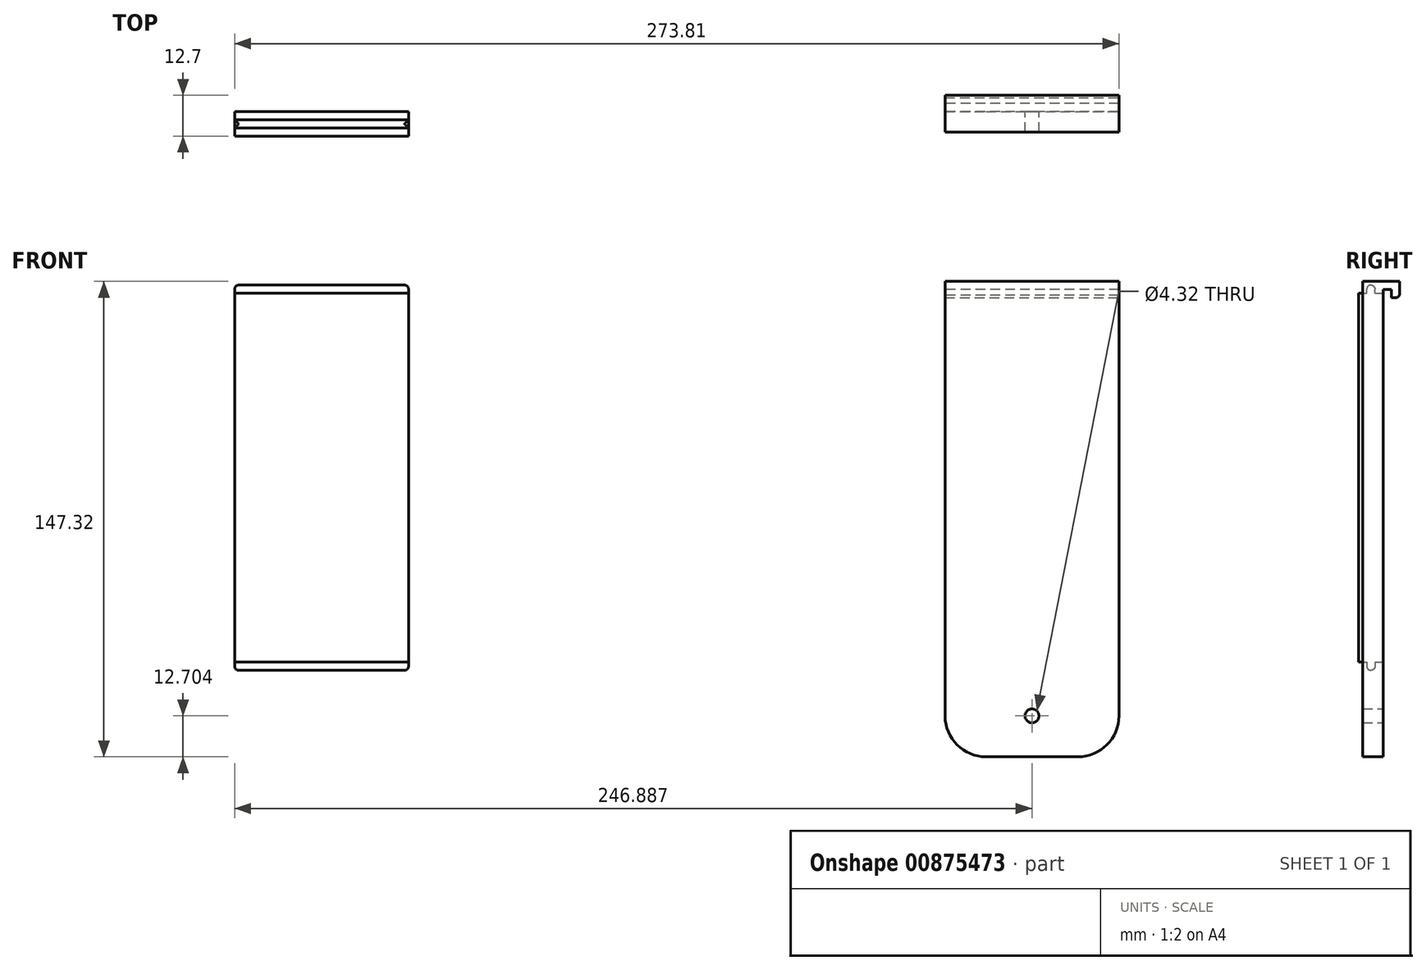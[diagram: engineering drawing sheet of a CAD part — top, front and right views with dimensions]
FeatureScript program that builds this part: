
annotation { "Feature Type Name" : "Feature", "Feature Type Description" : "" }
export const myFeature = defineFeature(function(context is Context, id is Id, definition is map)
    precondition{}
    {
        {
            var Q0;
            Q0=qCreatedBy(makeId("Front.planeOp"),FACE);
            var sketch = newSketch(context, id + "F0", { "sketchPlane" : qUnion([Q0])});
            skLineSegment(sketch, "E0.bottom", {"start": v(-137.16, 59.7) * mm, "end": v(-83.32, 59.7) * mm});
            skLineSegment(sketch, "E0.top", {"start": v(-137.16, -54.6) * mm, "end": v(-83.32, -54.6) * mm});
            skLineSegment(sketch, "E0.left", {"start": v(-137.16, 59.7) * mm, "end": v(-137.16, -54.6) * mm});
            skLineSegment(sketch, "E0.right", {"start": v(-83.32, 59.7) * mm, "end": v(-83.32, -54.6) * mm});
            skSolve(sketch);
        }
        {
            var Q0;
            Q0=makeQuery(id+"F0.imprint","IMPRINT",FACE,{"disambiguationData":[TD([[makeQuery(id+"F0.imprint","IMPRINT",EDGE,{"derivedFrom":sQuery(id+"F0.wireOp",EDGE,"E0.bottom")}),-1.0]])]});
            extrude(context, id + "F1", {"entities" : qUnion([Q0]), "depth" : 7.62 * mm, "offsetDistance" : 25.4 * mm});
        }
        {
            var Q0;
            Q0=makeQuery(id+"F1.opExtrude","SWEPT_FACE",FACE,{"disambiguationData":[OSD([sQuery(id+"F0.wireOp",EDGE,"E0.left")])]});
            var sketch = newSketch(context, id + "F2", { "sketchPlane" : qUnion([Q0])});
            skLineSegment(sketch, "E1.bottom", {"start": v(2.54, -54.6) * mm, "end": v(5.08, -54.6) * mm});
            skLineSegment(sketch, "E1.top", {"start": v(2.54, -57.13) * mm, "end": v(5.08, -57.13) * mm});
            skLineSegment(sketch, "E1.left", {"start": v(2.54, -54.6) * mm, "end": v(2.54, -57.13) * mm});
            skLineSegment(sketch, "E1.right", {"start": v(5.08, -54.6) * mm, "end": v(5.08, -57.13) * mm});
            skLineSegment(sketch, "E2.bottom", {"start": v(2.54, 59.7) * mm, "end": v(5.08, 59.7) * mm});
            skLineSegment(sketch, "E2.top", {"start": v(2.54, 62.25) * mm, "end": v(5.08, 62.25) * mm});
            skLineSegment(sketch, "E2.left", {"start": v(2.54, 59.7) * mm, "end": v(2.54, 62.25) * mm});
            skLineSegment(sketch, "E2.right", {"start": v(5.08, 59.7) * mm, "end": v(5.08, 62.25) * mm});
            skSolve(sketch);
        }
        {
            var Q0;
            Q0=makeQuery(id+"F2.imprint","IMPRINT",FACE,{"disambiguationData":[TD([[makeQuery(id+"F2.imprint","IMPRINT",EDGE,{"derivedFrom":sQuery(id+"F2.wireOp",EDGE,"E1.bottom")}),1.0]])]});
            var Q1;
            Q1=makeQuery(id+"F2.imprint","IMPRINT",FACE,{"disambiguationData":[TD([[makeQuery(id+"F2.imprint","IMPRINT",EDGE,{"derivedFrom":sQuery(id+"F2.wireOp",EDGE,"E2.bottom")}),-1.0]])]});
            extrude(context, id + "F3", {"entities" : qUnion([Q0, Q1]), "operationType" : NewBodyOperationType.ADD, "oppositeDirection" : true, "depth" : 53.85 * mm, "offsetDistance" : 25.4 * mm});
        }
        {
            var Q0;
            Q0=makeQuery(id+"F3.opExtrude","SWEPT_EDGE",EDGE,{"disambiguationData":[OSD([sQuery(id+"F2.wireOp",EDGE,"E2.top"),sQuery(id+"F2.wireOp",EDGE,"E2.left")])]});
            var Q1;
            Q1=makeQuery(id+"F3.opExtrude","SWEPT_EDGE",EDGE,{"disambiguationData":[OSD([sQuery(id+"F2.wireOp",EDGE,"E2.top"),sQuery(id+"F2.wireOp",EDGE,"E2.right")])]});
            var Q2;
            Q2=makeQuery(id+"F3.opExtrude","CAP_EDGE",EDGE,{"disambiguationData":[OSD([sQuery(id+"F2.wireOp",EDGE,"E2.top")])],"isStart":true});
            var Q3;
            Q3=makeQuery(id+"F3.opExtrude","CAP_EDGE",EDGE,{"disambiguationData":[OSD([sQuery(id+"F2.wireOp",EDGE,"E2.top")])],"isStart":false});
            fillet(context, id + "F4", {"entities" : qUnion([Q0, Q1, Q2, Q3]), "radius" : 1.27 * mm, "tangentPropagation" : true, "allowEdgeOverflow" : false});
        }
        {
            var Q0;
            Q0=makeQuery(id+"F3.opExtrude","SWEPT_EDGE",EDGE,{"disambiguationData":[OSD([sQuery(id+"F2.wireOp",EDGE,"E1.top"),sQuery(id+"F2.wireOp",EDGE,"E1.right")])]});
            var Q1;
            Q1=makeQuery(id+"F3.opExtrude","SWEPT_EDGE",EDGE,{"disambiguationData":[OSD([sQuery(id+"F2.wireOp",EDGE,"E1.top"),sQuery(id+"F2.wireOp",EDGE,"E1.left")])]});
            var Q2;
            Q2=makeQuery(id+"F3.opExtrude","CAP_EDGE",EDGE,{"disambiguationData":[OSD([sQuery(id+"F2.wireOp",EDGE,"E1.top")])],"isStart":false});
            var Q3;
            Q3=makeQuery(id+"F3.opExtrude","CAP_EDGE",EDGE,{"disambiguationData":[OSD([sQuery(id+"F2.wireOp",EDGE,"E1.top")])],"isStart":true});
            fillet(context, id + "F5", {"entities" : qUnion([Q0, Q1, Q2, Q3]), "radius" : 1.27 * mm, "tangentPropagation" : true, "allowEdgeOverflow" : false});
        }
        {
            var Q0;
            Q0=qCreatedBy(makeId("Front.planeOp"),FACE);
            var sketch = newSketch(context, id + "F6", { "sketchPlane" : qUnion([Q0])});
            skLineSegment(sketch, "E3.bottom", {"start": v(82.8, -83.95) * mm, "end": v(136.65, -83.95) * mm});
            skLineSegment(sketch, "E3.top", {"start": v(82.8, 63.37) * mm, "end": v(136.65, 63.37) * mm});
            skLineSegment(sketch, "E3.left", {"start": v(82.8, -83.95) * mm, "end": v(82.8, 63.37) * mm});
            skLineSegment(sketch, "E3.right", {"start": v(136.65, -83.95) * mm, "end": v(136.65, 63.37) * mm});
            skSolve(sketch);
        }
        {
            var Q0;
            Q0=makeQuery(id+"F6.imprint","IMPRINT",FACE,{"disambiguationData":[TD([[makeQuery(id+"F6.imprint","IMPRINT",EDGE,{"derivedFrom":sQuery(id+"F6.wireOp",EDGE,"E3.bottom")}),1.0]])]});
            extrude(context, id + "F7", {"entities" : qUnion([Q0]), "depth" : 6.35 * mm, "offsetDistance" : 25.4 * mm});
        }
        {
            var Q0;
            Q0=makeQuery(id+"F7.opExtrude","SWEPT_EDGE",EDGE,{"disambiguationData":[OSD([sQuery(id+"F6.wireOp",EDGE,"E3.bottom"),sQuery(id+"F6.wireOp",EDGE,"E3.right")])]});
            var Q1;
            Q1=makeQuery(id+"F7.opExtrude","SWEPT_EDGE",EDGE,{"disambiguationData":[OSD([sQuery(id+"F6.wireOp",EDGE,"E3.bottom"),sQuery(id+"F6.wireOp",EDGE,"E3.left")])]});
            fillet(context, id + "F8", {"entities" : qUnion([Q0, Q1]), "radius" : 12.7 * mm, "tangentPropagation" : true, "allowEdgeOverflow" : false});
        }
        {
            var Q0;
            Q0=makeQuery(id+"F7.opExtrude","CAP_FACE",FACE,{"disambiguationData":[OSD([sQuery(id+"F6.wireOp",EDGE,"E3.bottom"),sQuery(id+"F6.wireOp",EDGE,"E3.top"),sQuery(id+"F6.wireOp",EDGE,"E3.left"),sQuery(id+"F6.wireOp",EDGE,"E3.right")])],"isStart":true});
            var sketch = newSketch(context, id + "F9", { "sketchPlane" : qUnion([Q0])});
            skLineSegment(sketch, "E4.bottom", {"start": v(-82.8, 63.37) * mm, "end": v(-136.65, 63.37) * mm});
            skLineSegment(sketch, "E4.top", {"start": v(-82.8, 58.3) * mm, "end": v(-136.65, 58.3) * mm});
            skLineSegment(sketch, "E4.left", {"start": v(-82.8, 63.37) * mm, "end": v(-82.8, 58.3) * mm});
            skLineSegment(sketch, "E4.right", {"start": v(-136.65, 63.37) * mm, "end": v(-136.65, 58.3) * mm});
            skSolve(sketch);
        }
        {
            var Q0;
            Q0=makeQuery(id+"F9.imprint","IMPRINT",FACE,{"disambiguationData":[TD([[makeQuery(id+"F9.imprint","IMPRINT",EDGE,{"derivedFrom":sQuery(id+"F9.wireOp",EDGE,"E4.bottom")}),1.0]])]});
            extrude(context, id + "F10", {"entities" : qUnion([Q0]), "operationType" : NewBodyOperationType.ADD, "depth" : 5.08 * mm, "offsetDistance" : 25.4 * mm});
        }
        {
            var Q0;
            Q0=makeQuery(id+"F10.boolean.opBoolean","MERGE",FACE,{"derivedFrom":[makeQuery(id+"F7.opExtrude","SWEPT_FACE",FACE,{"disambiguationData":[OSD([sQuery(id+"F6.wireOp",EDGE,"E3.left")])]}),makeQuery(id+"F10.opExtrude","SWEPT_FACE",FACE,{"disambiguationData":[OSD([sQuery(id+"F9.wireOp",EDGE,"E4.left")])]})]});
            var sketch = newSketch(context, id + "F11", { "sketchPlane" : qUnion([Q0])});
            skLineSegment(sketch, "E5.bottom", {"start": v(0, 60.83) * mm, "end": v(-2.54, 60.83) * mm});
            skLineSegment(sketch, "E5.top", {"start": v(0, 58.3) * mm, "end": v(-2.54, 58.3) * mm});
            skLineSegment(sketch, "E5.left", {"start": v(0, 60.83) * mm, "end": v(0, 58.3) * mm});
            skLineSegment(sketch, "E5.right", {"start": v(-2.54, 60.83) * mm, "end": v(-2.54, 58.3) * mm});
            skSolve(sketch);
        }
        {
            var Q0;
            Q0=makeQuery(id+"F11.imprint","IMPRINT",FACE,{"disambiguationData":[TD([[makeQuery(id+"F11.imprint","IMPRINT",EDGE,{"derivedFrom":sQuery(id+"F11.wireOp",EDGE,"E5.bottom")}),1.0]])]});
            extrude(context, id + "F12", {"entities" : qUnion([Q0]), "operationType" : NewBodyOperationType.REMOVE, "oppositeDirection" : true, "depth" : 76.2 * mm, "offsetDistance" : 25.4 * mm});
        }
        {
            var Q0;
            Q0=makeQuery(id+"F10.opExtrude","CAP_EDGE",EDGE,{"disambiguationData":[OSD([sQuery(id+"F9.wireOp",EDGE,"E4.top")])],"isStart":false});
            chamfer(context, id + "F13", {"entities" : qUnion([Q0]), "width" : 0.76 * mm, "tangentPropagation" : true});
        }
        {
            var Q0;
            Q0=makeQuery(id+"F12.boolean.opBoolean","MERGE",FACE,{"derivedFrom":[makeQuery(id+"F7.opExtrude","CAP_FACE",FACE,{"disambiguationData":[OSD([sQuery(id+"F6.wireOp",EDGE,"E3.bottom"),sQuery(id+"F6.wireOp",EDGE,"E3.top"),sQuery(id+"F6.wireOp",EDGE,"E3.left"),sQuery(id+"F6.wireOp",EDGE,"E3.right")])],"isStart":true})],"fromTools":[makeQuery(id+"F12.opExtrude","SWEPT_FACE",FACE,{"disambiguationData":[OSD([sQuery(id+"F11.wireOp",EDGE,"E5.left")])]})]});
            var sketch = newSketch(context, id + "F14", { "sketchPlane" : qUnion([Q0])});
            skCircle(sketch, "E6", {"center": v(-109.73, -71.25) * mm, "radius": 2.16 * mm});
            skSolve(sketch);
        }
        {
            var Q0;
            Q0=makeQuery(id+"F14.imprint","IMPRINT",FACE,{"disambiguationData":[TD([[makeQuery(id+"F14.imprint","IMPRINT",EDGE,{"derivedFrom":sQuery(id+"F14.wireOp",EDGE,"E6")}),1.0]])]});
            extrude(context, id + "F15", {"entities" : qUnion([Q0]), "operationType" : NewBodyOperationType.REMOVE, "oppositeDirection" : true, "depth" : 25.4 * mm, "offsetDistance" : 25.4 * mm});
        }
    });
